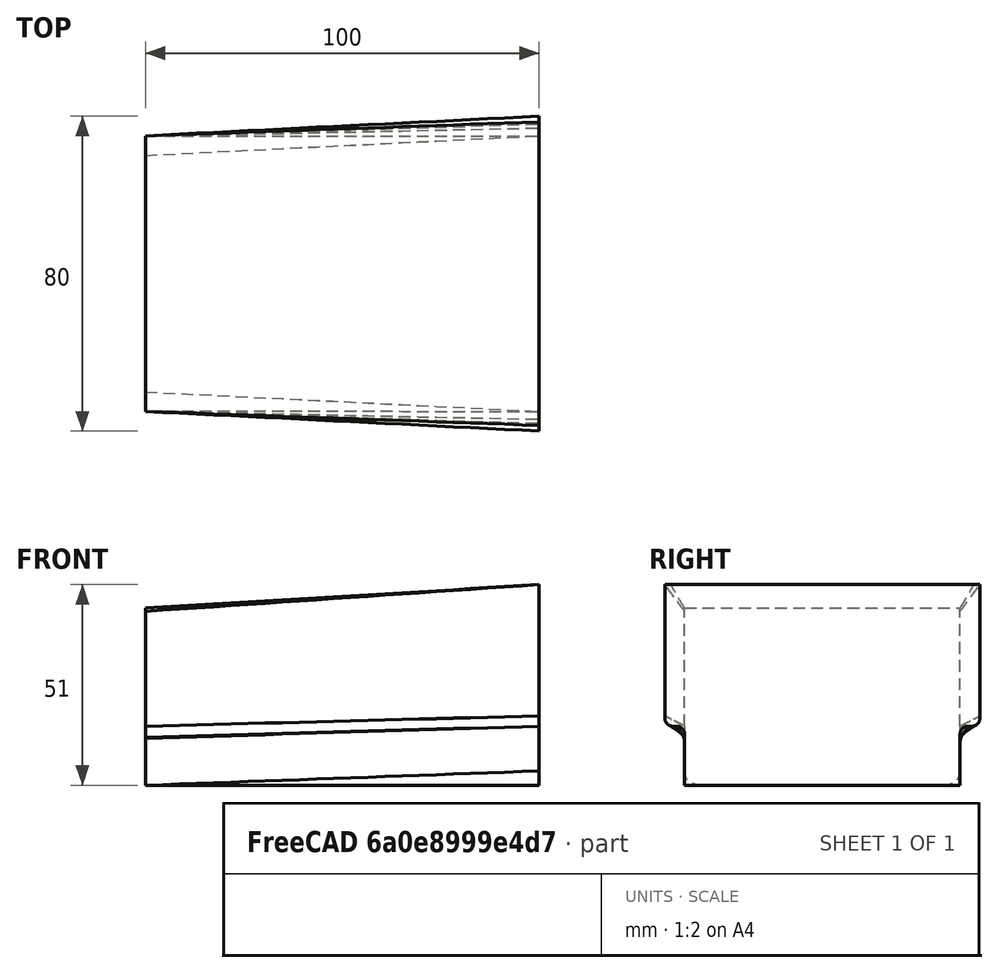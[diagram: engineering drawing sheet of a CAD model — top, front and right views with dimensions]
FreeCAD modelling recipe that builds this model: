
FCSTD DOCUMENT  (FreeCAD 0.19R24267 (Git))
Label: loft_test
License: All rights reserved
LicenseURL: http://en.wikipedia.org/wiki/All_rights_reserved
objects: Sketcher::SketchObject×2, PartDesign::AdditiveLoft×1, PartDesign::Body×1
note: 5 computed .brp shape members not serialized (recipe doc carries the construction recipe); baked Part::Feature solids carry a one-line shape summary decoded from their .brp

FEATURE [Sketcher::SketchObject] Sketch
  AttachmentOffset = pos=(0,0,-50) rot=(0,0,1;0rad)
  FullyConstrained = true
  MapMode = 5
  Placement = pos=(-50,1.11e-14,-1.11e-14) rot=(0.57735,0.57735,0.57735;2.0944rad)
  Support = -> [YZ_Plane]
  sketch-geometry (8):
    g0: LineSegment StartX=-35 StartY=30 StartZ=0 EndX=35 EndY=30 EndZ=0
    g1: LineSegment StartX=34.9 StartY=0 StartZ=0 EndX=34.9 EndY=-15 EndZ=0
    g2: LineSegment StartX=34.9 StartY=-15 StartZ=0 EndX=-34.9 EndY=-15 EndZ=0
    g3: LineSegment StartX=-34.9 StartY=-15 StartZ=0 EndX=-34.9 EndY=0 EndZ=0
    g4: LineSegment StartX=-34.9 StartY=0 StartZ=0 EndX=-35 EndY=0 EndZ=0
    g5: LineSegment StartX=-35 StartY=0 StartZ=0 EndX=-35 EndY=30 EndZ=0
    g6: LineSegment StartX=34.9 StartY=0 StartZ=0 EndX=35 EndY=0 EndZ=0
    g7: LineSegment StartX=35 StartY=0 StartZ=0 EndX=35 EndY=30 EndZ=0
  constraints (23):
    c: Horizontal(g0)
    c: PointOnObject(g1,g-1)
    c: Vertical(g1)
    c: Coincident(g1,g2)
    c: Horizontal(g2)
    c: Coincident(g2,g3)
    c: Vertical(g3)
    c: Symmetric(g3,g1,g-1)
    c: DistanceY(g1,g1) = 15
    c: DistanceX(g0,g0) = 70
    c: DistanceY(g1,g0) = 30
    c: Coincident(g4,g3)
    c: PointOnObject(g4,g-1)
    c: Coincident(g5,g4)
    c: Vertical(g5)
    c: Coincident(g6,g1)
    c: PointOnObject(g6,g-1)
    c: Coincident(g7,g6)
    c: Coincident(g7,g0)
    c: Equal(g4,g6)
    c: Coincident(g5,g0)
    c: Equal(g7,g5)
    c: DistanceX(g6,g6) = 0.1
FEATURE [Sketcher::SketchObject] Sketch001
  AttachmentOffset = pos=(0,0,50) rot=(0,0,1;0rad)
  FullyConstrained = true
  MapMode = 5
  Placement = pos=(50,-1.11e-14,1.11e-14) rot=(0.57735,0.57735,0.57735;2.0944rad)
  Support = -> [YZ_Plane]
  sketch-geometry (12):
    g0: LineSegment StartX=-40 StartY=36 StartZ=0 EndX=40 EndY=36 EndZ=0
    g1: LineSegment StartX=40 StartY=36 StartZ=0 EndX=40 EndY=2 EndZ=0
    g2: LineSegment StartX=35 StartY=-15 StartZ=0 EndX=-35 EndY=-15 EndZ=0
    g3: LineSegment StartX=-40 StartY=2 StartZ=0 EndX=-40 EndY=36 EndZ=0
    g4: LineSegment StartX=-38 StartY=1.67e-14 StartZ=0 EndX=-37 EndY=1.68e-14 EndZ=0
    g5: LineSegment StartX=-35 StartY=-2 StartZ=0 EndX=-35 EndY=-15 EndZ=0
    g6: LineSegment StartX=38 StartY=0 StartZ=0 EndX=37 EndY=1.91e-14 EndZ=0
    g7: LineSegment StartX=35 StartY=-2 StartZ=0 EndX=35 EndY=-15 EndZ=0
    g8: ArcOfCircle CenterX=-37 CenterY=-2 CenterZ=0 NormalX=0 NormalY=0 NormalZ=1 AngleXU=0 Radius=2 StartAngle=0 EndAngle=1.5708
    g9: ArcOfCircle CenterX=37 CenterY=-2 CenterZ=0 NormalX=0 NormalY=0 NormalZ=1 AngleXU=0 Radius=2 StartAngle=1.5708 EndAngle=3.14159
    g10: ArcOfCircle CenterX=-38 CenterY=2 CenterZ=0 NormalX=0 NormalY=0 NormalZ=1 AngleXU=0 Radius=2 StartAngle=3.14159 EndAngle=4.71239
    g11: ArcOfCircle CenterX=38 CenterY=2 CenterZ=0 NormalX=0 NormalY=0 NormalZ=1 AngleXU=0 Radius=2 StartAngle=4.71239 EndAngle=6.28319
  constraints (31):
    c: Horizontal(g0)
    c: Coincident(g0,g1)
    c: Vertical(g1)
    c: Coincident(g3,g0)
    c: Vertical(g3)
    c: DistanceX(g0,g0) = 80
    c: Coincident(g5,g2)
    c: Coincident(g7,g2)
    c: DistanceX(g2,g2) = 70
    c: Vertical(g7)
    c: Vertical(g5)
    c: DistanceY(g2,g-1) = 15
    c: Tangent(g4,g8) = 1.5708
    c: Tangent(g5,g8) = 1.5708
    c: Tangent(g7,g9) = -1.5708
    c: Tangent(g6,g9) = -1.5708
    c: Equal(g8,g9)
    c: Equal(g6,g4)
    c: Equal(g7,g5)
    c: Vertical(g8,g4)
    c: Radius(g8) = 2
    c: Tangent(g3,g10) = 1.5708
    c: Tangent(g4,g10) = -1.5708
    c: Equal(g8,g10)
    c: Tangent(g1,g11) = 1.5708
    c: Tangent(g6,g11) = 1.5708
    c: Equal(g11,g9)
    c: Vertical(g6,g11)
    c: DistanceY(g-1,g0) = 36
    c: PointOnObject(g6,g-1)
    c: Symmetric(g2,g2,g-2)
FEATURE [PartDesign::AdditiveLoft] AdditiveLoft
  Closed = false
  Placement = pos=(0,0,0) rot=(0.57735,0.57735,0.57735;2.0944rad)
  Profile = -> Sketch
  Ruled = false
  Sections = -> [Sketch001]
FEATURE [PartDesign::Body] Body
  Group = -> [Sketch,Sketch001,AdditiveLoft]
  Origin = -> Origin
  Tip = -> AdditiveLoft
